FCSTD DOCUMENT  (FreeCAD 0.20R27428 (Git))
Label: Muster-datei
License: All rights reserved
LicenseURL: http://en.wikipedia.org/wiki/All_rights_reserved
objects: Spreadsheet::Sheet×1, PartDesign::Body×1
note: 1 computed .brp shape members not serialized (recipe doc carries the construction recipe); baked Part::Feature solids carry a one-line shape summary decoded from their .brp

FEATURE [Spreadsheet::Sheet] Spreadsheet
  cells = A1=alle Werte sind in mm angegeben; A3=Standardparameter; A4=Wandstärke; B4(STD_wandstaerke)=2; C4=standardmäßige Wandstärke; A5=Toleranz allgemein; B5(STD_toleranz_allg)=0.1; C5=Toleranz beim Drucken, wird abgezogen, hinzuaddiert, um z.B. Nut und Feder herstellen zu können; A6=Toleranz Spielpassung; B6(STD_toleranz_spiel)=0.25; C6=Welle in einer Bohrung hat Spiel; F6=Maß eines Abstands zwischen Teilen; H6=Welle ist also  z.B. 2 * STD_toleranz_spiel kleiner als Bohrung; A7=Toleranz Übergangspassung; B7(STD_toleranz_pass)=0.1; C7=Welle sitzt zentrisch einer Bohrung und kann sich "spielfrei" drehen; A8=Toleranz Presspassung; B8(STD_toleranz_press)=0.05; C8=Welle sitzt fest in einer Bohrung (wird reingepresst) und kan sich nicht drehen; A10=fremde Maße; C10=Diese Maßangaben stammen von Teilen, die nicht im CAD Objekt enthalten sind, an die aber z.B. die 3D Druckteile angeschlossen werden.; A11=<Maßangaben Gruppe 1>; A12=fremdes Maß 1; B12(FM_mass1)=; A23=Maße im Modell; A24=<Maßangaben Gruppe 1>; A25=eigens Maß 1; B25(eigenes_Mass_1)=; A37=Schraubenmaße metrisch ISO; A38=Schrauben; B38=Außenmaß; C38=Kernloch-⌀; D38=Durchgangsloch-⌀; A39=M 1; B39(m1_aussen)=1; C39(m1_kernloch)=0.75; D39(m1_durchgang)=1.2; A40=M 2; B40(m2_aussen)=2; C40(m2_kernloch)=1.6; D40(m2_durchgang)=2.4; A41=M 3; B41(m3_aussen)=3; C41(m3_kernloch)=2.5; D41(m3_durchgang)=3.4; A42=M 4; B42(m4_aussen)=4; C42(m4_kernloch)=3.3; D42(m4_durchgang)=4.5; A43=M 5; B43(m5_aussen)=5; C43(m5_kernloch)=4.2; D43(m5_durchgang)=5.5; A44=M 6; B44(m6_aussen)=6; C44(m6_kernloch)=5; D44(m6_durchgang)=6.6; A45=M 8; B45(m8_aussen)=8; C45(m8_kernloch)=6.8; D45(m8_durchgang)=9; A46=M 10; B46(m10_aussen)=10; C46(m10_kernloch)=8.5; D46(m10_durchgang)=11; A47=M 12; B47(m12_aussen)=12; C47(m12_kernloch)=10.2; D47(m12_durchgang)=13.5; A48=M 16; B48(m16_aussen)=16; C48(m16_kernloch)=14; D48(m16_durchgang)=17.5; A49=M 20; B49(m20_aussen)=20; C49(m20_kernloch)=17.5; D49(m20_durchgang)=22; A50=M 24; B50(m24_aussen)=24; C50(m24_kernloch)=21; D50(m24_durchgang)=26; A51=M 30; B51(m30_aussen)=30; C51(m30_kernloch)=26.5; D51(m30_durchgang)=33; A52=M 36; B52(m36_aussen)=36; C52(m36_kernloch)=32; D52(m36_durchgang)=39; A53=M 42; B53(m42_aussen)=42; C53(m42_kernloch)=37.5; D53(m42_durchgang)=45; A54=M 48; B54(m48_aussen)=48; C54(m48_kernloch)=43; D54(m48_durchgang)=52; A55=M 56; B55(m56_aussen)=56; C55(m56_kernloch)=50.5; D55(m56_durchgang)=62; A56=M 64; B56(m64_aussen)=64; C56(m64_kernloch)=58; D56(m64_durchgang)=70
FEATURE [PartDesign::Body] Body
  Origin = -> Origin
